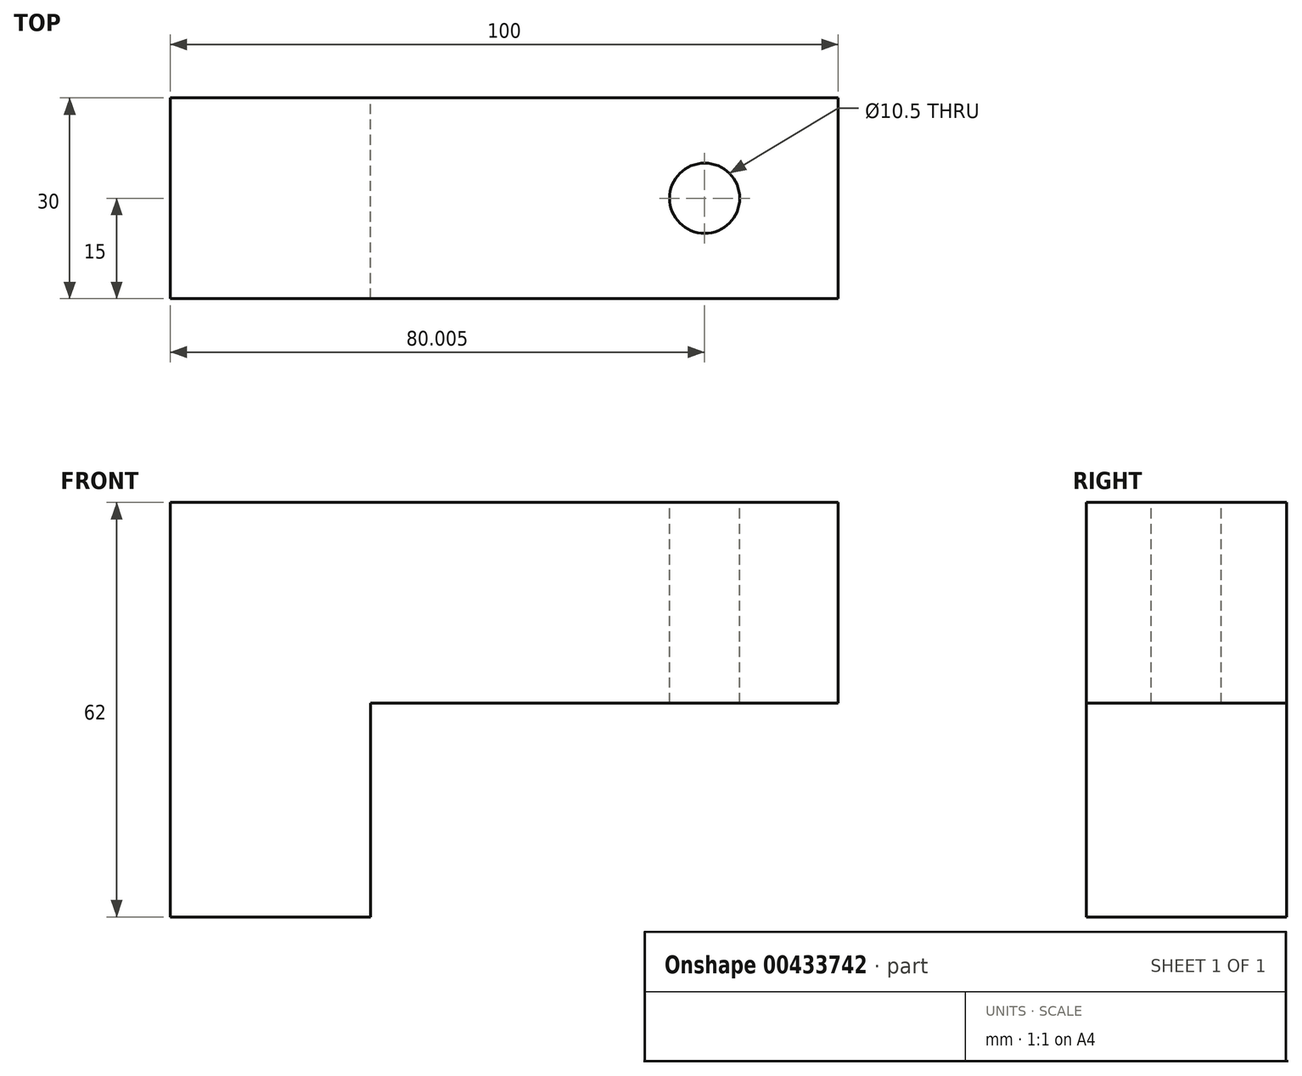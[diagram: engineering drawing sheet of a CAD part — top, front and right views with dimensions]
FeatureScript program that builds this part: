
annotation { "Feature Type Name" : "Feature", "Feature Type Description" : "" }
export const myFeature = defineFeature(function(context is Context, id is Id, definition is map)
    precondition{}
    {
        {
            var Q0;
            Q0=qCreatedBy(makeId("Front.planeOp"),FACE);
            var sketch = newSketch(context, id + "F0", { "sketchPlane" : qUnion([Q0])});
            skLineSegment(sketch, "E0.bottom", {"start": v(-37.88, -19.26) * mm, "end": v(-7.88, -19.26) * mm});
            skLineSegment(sketch, "E0.top", {"start": v(-37.88, 12.74) * mm, "end": v(-7.88, 12.74) * mm});
            skLineSegment(sketch, "E0.left", {"start": v(-37.88, -19.26) * mm, "end": v(-37.88, 12.74) * mm});
            skLineSegment(sketch, "E0.right", {"start": v(-7.88, -19.26) * mm, "end": v(-7.88, 12.74) * mm});
            skLineSegment(sketch, "E1.bottom", {"start": v(-37.88, 12.74) * mm, "end": v(62.12, 12.74) * mm});
            skLineSegment(sketch, "E1.top", {"start": v(-37.88, 42.74) * mm, "end": v(62.12, 42.74) * mm});
            skLineSegment(sketch, "E1.left", {"start": v(-37.88, 12.74) * mm, "end": v(-37.88, 42.74) * mm});
            skLineSegment(sketch, "E1.right", {"start": v(62.12, 12.74) * mm, "end": v(62.12, 42.74) * mm});
            skSolve(sketch);
        }
        {
            var Q0;
            Q0 = qSketchRegion(id + "F0", true);
            extrude(context, id + "F1", {"entities" : qUnion([Q0]), "depth" : 30 * mm, "offsetDistance" : 25 * mm});
        }
        {
            var Q0;
            Q0=makeQuery(id+"F1.opExtrude","SWEPT_FACE",FACE,{"disambiguationData":[OSD([sQuery(id+"F0.wireOp",EDGE,"E1.top")])]});
            var sketch = newSketch(context, id + "F2", { "sketchPlane" : qUnion([Q0])});
            skCircle(sketch, "E2", {"center": v(42.12, -15) * mm, "radius": 5.5 * mm});
            skSolve(sketch);
        }
        {
            var Q0;
            Q0=sQuery(id+"F2.wireOp",VERTEX,"E2.center");
            var Q1;
            Q1=makeQuery(id+"F1.opExtrude","SWEPT_BODY",BODY,{"disambiguationData":[OSD([sQuery(id+"F0.wireOp",EDGE,"E0.bottom"),sQuery(id+"F0.wireOp",EDGE,"E0.left"),sQuery(id+"F0.wireOp",EDGE,"E0.right"),sQuery(id+"F0.wireOp",EDGE,"E1.bottom"),sQuery(id+"F0.wireOp",EDGE,"E1.top"),sQuery(id+"F0.wireOp",EDGE,"E1.left"),sQuery(id+"F0.wireOp",EDGE,"E1.right")])]});
            hole(context, id + "F3", {"style" : HoleStyle.SIMPLE, "endStyle" : HoleEndStyle.THROUGH, "holeDiameter" : 10.5 * mm, "majorDiameter" : 5 * mm, "isTappedThrough" : true, "tappedDepth" : 12 * mm, "tapClearance" : 3, "locations" : qUnion([Q0]), "scope" : qUnion([Q1])});
        }
    });
